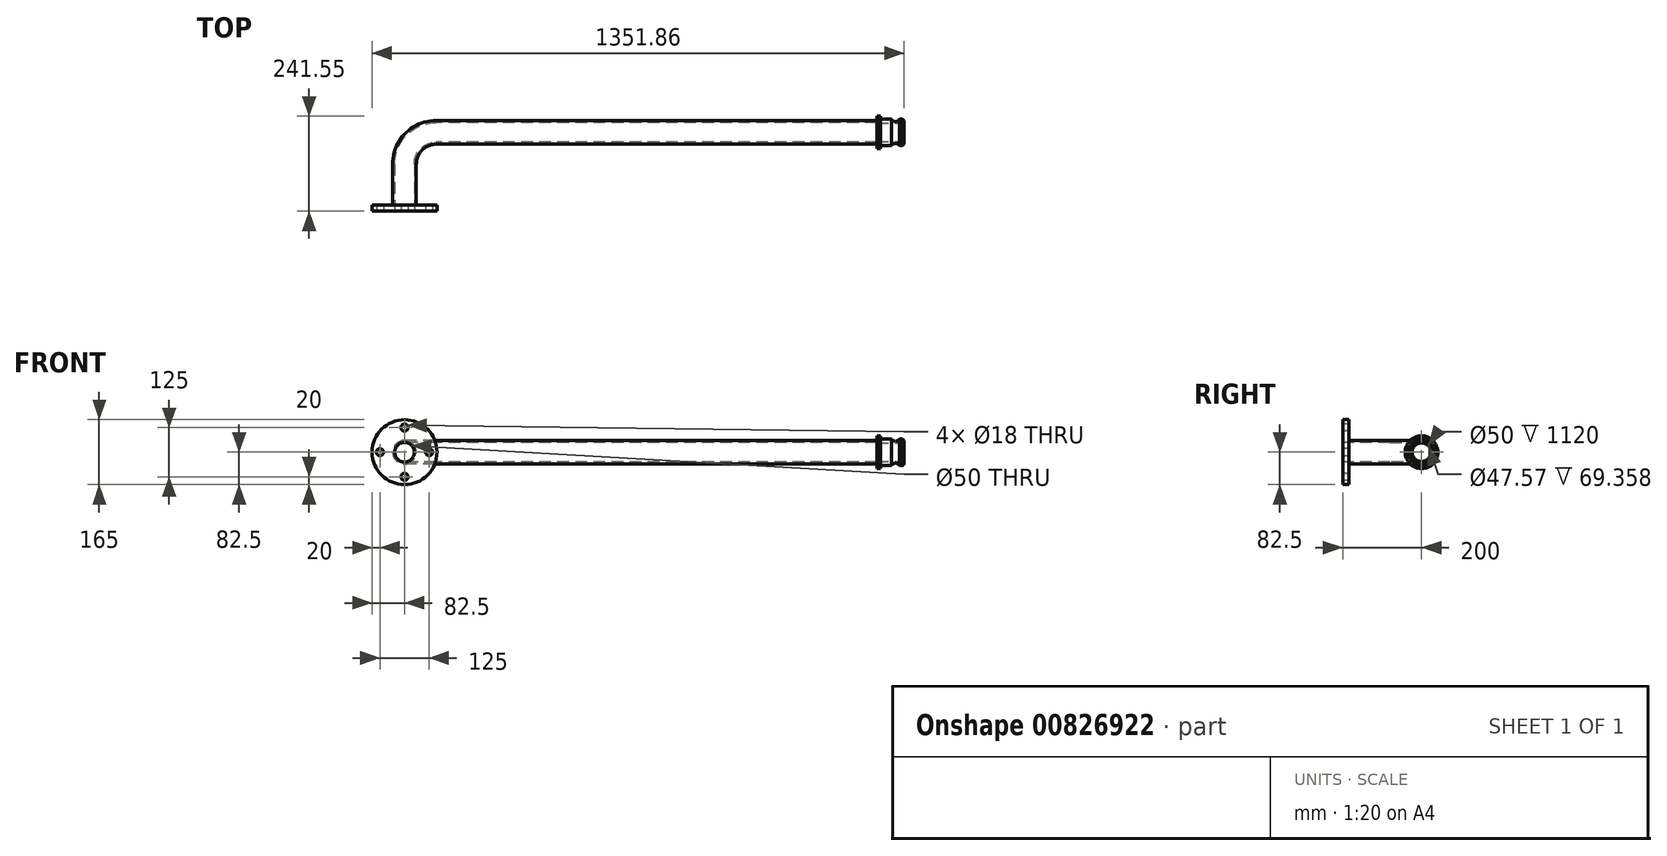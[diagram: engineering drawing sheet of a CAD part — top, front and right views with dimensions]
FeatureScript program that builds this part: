
annotation { "Feature Type Name" : "Feature", "Feature Type Description" : "" }
export const myFeature = defineFeature(function(context is Context, id is Id, definition is map)
    precondition{}
    {
        {
            var Q0;
            Q0=qCreatedBy(makeId("Top.planeOp"),FACE);
            var sketch = newSketch(context, id + "F0", { "sketchPlane" : qUnion([Q0])});
            skLineSegment(sketch, "E0", {"start": v(0, 0) * mm, "end": v(-1120, 0) * mm});
            skLineSegment(sketch, "E1", {"start": v(-1200, -80) * mm, "end": v(-1200, -200) * mm});
            skPoint(sketch, "E2.visualSharp", {"position": v(-1200, 0) * mm});
            skArc(sketch, "E2.filletArc", {"start": v(-1120, 0) * mm, "mid": v(-1176.57, -23.43) * mm, "end": v(-1200, -80) * mm});
            skSolve(sketch);
        }
        {
            var Q0;
            Q0=qCreatedBy(makeId("Right.planeOp"),FACE);
            var sketch = newSketch(context, id + "F1", { "sketchPlane" : qUnion([Q0])});
            skCircle(sketch, "E3", {"center": v(0, 0) * mm, "radius": 25 * mm});
            skCircle(sketch, "E4", {"center": v(0, 0) * mm, "radius": 30 * mm});
            skSolve(sketch);
        }
        {
            var Q0;
            Q0=makeQuery(id+"F1.imprint","IMPRINT",FACE,{"disambiguationData":[TD([[makeQuery(id+"F1.imprint","IMPRINT",EDGE,{"derivedFrom":sQuery(id+"F1.wireOp",EDGE,"E3")}),-1.0]])]});
            var Q1;
            Q1=sQuery(id+"F0.wireOp",EDGE,"E0");
            var Q2;
            Q2=sQuery(id+"F0.wireOp",EDGE,"E2.filletArc");
            var Q3;
            Q3=sQuery(id+"F0.wireOp",EDGE,"E1");
            sweep(context, id + "F2", {"profiles" : qUnion([Q0]), "path" : qUnion([Q1, Q2, Q3])});
        }
        {
            var Q0;
            Q0=makeQuery(id+"F2.opSweep","CAP_FACE",FACE,{"disambiguationData":[OSD([sQuery(id+"F0.wireOp",VERTEX,"E1.end"),sQuery(id+"F1.wireOp",EDGE,"E3"),sQuery(id+"F1.wireOp",EDGE,"E4")])],"isStart":false});
            var sketch = newSketch(context, id + "F3", { "sketchPlane" : qUnion([Q0])});
            skCircle(sketch, "E5", {"center": v(-1200, 0) * mm, "radius": 82.5 * mm});
            skCircle(sketch, "E6", {"center": v(-1200, 62.5) * mm, "radius": 9 * mm});
            skCircle(sketch, "E7.0", {"center": v(-1200, 0) * mm, "radius": 25 * mm});
            skCircle(sketch, "E8.1.0", {"center": v(-1262.5, 0) * mm, "radius": 9 * mm});
            skCircle(sketch, "E8.2.0", {"center": v(-1200, -62.5) * mm, "radius": 9 * mm});
            skCircle(sketch, "E8.3.0", {"center": v(-1137.5, 0) * mm, "radius": 9 * mm});
            skSolve(sketch);
        }
        {
            var Q0;
            Q0 = qSketchRegion(id + "F3", true);
            extrude(context, id + "F4", {"entities" : qUnion([Q0]), "operationType" : NewBodyOperationType.ADD, "oppositeDirection" : true, "depth" : 15 * mm, "offsetDistance" : 25 * mm});
        }
        {
            var Q0;
            Q0=qCreatedBy(makeId("Front.planeOp"),FACE);
            var sketch = newSketch(context, id + "F5", { "sketchPlane" : qUnion([Q0])});
            skLineSegment(sketch, "E9", {"start": v(-1120, 30) * mm, "end": v(0, 30) * mm});
            skLineSegment(sketch, "E10.0", {"start": v(0, -30) * mm, "end": v(0, 30) * mm});
            skLineSegment(sketch, "E11", {"start": v(0, -30) * mm, "end": v(-1120, -30) * mm});
            skLineSegment(sketch, "E12", {"start": v(0, 30) * mm, "end": v(0, 41.55) * mm});
            skLineSegment(sketch, "E13", {"start": v(0, 41.55) * mm, "end": v(9.2, 41.55) * mm});
            skLineSegment(sketch, "E14", {"start": v(9.2, 41.55) * mm, "end": v(9.2, 33.63) * mm});
            skLineSegment(sketch, "E15", {"start": v(9.2, 33.63) * mm, "end": v(37.17, 33.63) * mm});
            skArc(sketch, "E16", {"start": v(37.17, 33.63) * mm, "mid": v(47.29, 27.82) * mm, "end": v(57.4, 33.63) * mm});
            skLineSegment(sketch, "E17", {"start": v(57.4, 33.63) * mm, "end": v(65.31, 33.63) * mm});
            skLineSegment(sketch, "E18", {"start": v(65.31, 33.63) * mm, "end": v(69.36, 30.12) * mm});
            skLineSegment(sketch, "E19", {"start": v(69.36, 30.12) * mm, "end": v(69.36, 23.79) * mm});
            skLineSegment(sketch, "E20", {"start": v(69.36, 23.79) * mm, "end": v(0, 23.79) * mm});
            skLineSegment(sketch, "E21", {"start": v(0, 23.79) * mm, "end": v(0, 30) * mm});
            skSolve(sketch);
        }
        {
            var Q0;
            Q0=makeQuery(id+"F5.imprint","IMPRINT",FACE,{"disambiguationData":[TD([[makeQuery(id+"F5.imprint","IMPRINT",EDGE,{"derivedFrom":sQuery(id+"F5.wireOp",EDGE,"E12")}),-1.0]])]});
            var Q1;
            Q1=makeQuery(id+"F2.opSweep","SWEPT_FACE",FACE,{"disambiguationData":[OSD([sQuery(id+"F0.wireOp",EDGE,"E0"),sQuery(id+"F1.wireOp",EDGE,"E4")])]});
            revolve(context, id + "F6", {"operationType" : NewBodyOperationType.ADD, "surfaceOperationType" : NewSurfaceOperationType.NEW, "entities" : qUnion([Q0]), "axis" : qUnion([Q1]), "revolveType" : RevolveType.FULL});
        }
    });
